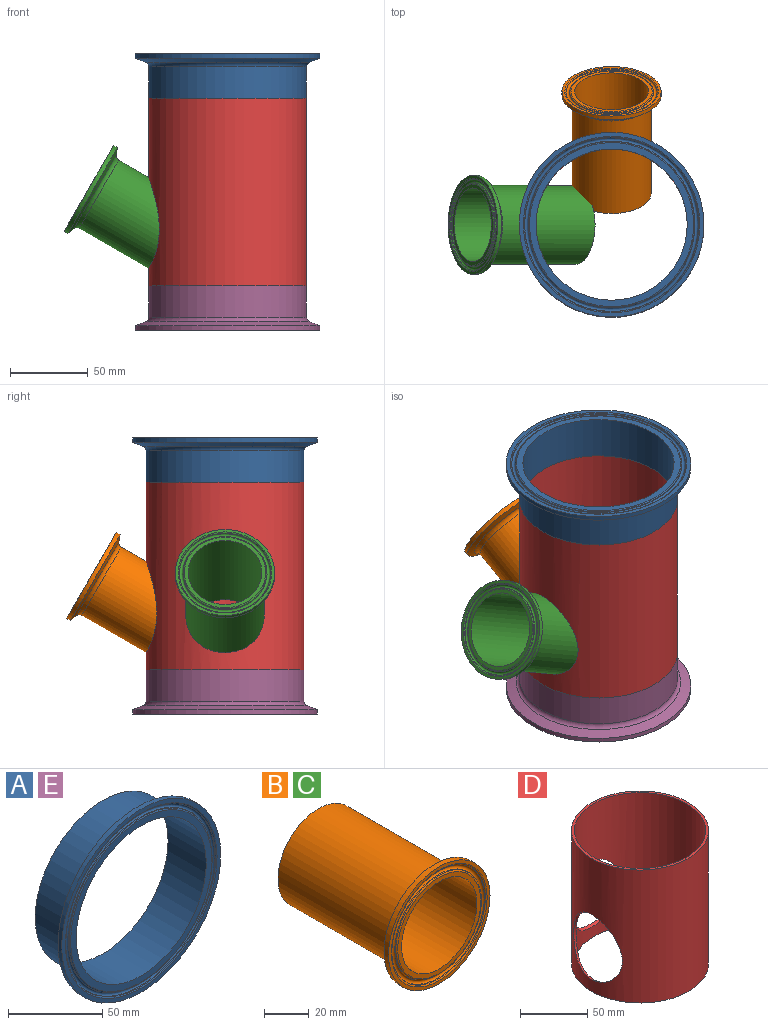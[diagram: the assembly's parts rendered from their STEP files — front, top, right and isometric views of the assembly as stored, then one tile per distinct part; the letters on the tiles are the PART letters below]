
ASSEMBLY  parts=5 mates=4
PART A: 13 faces, bbox 122.9x28.6x122.9 mm
  f0: cylinder r=59.46mm len=118.92mm, axis (0,-1,0), area 1062.8mm2, adj f1,f10
  f1: cone r=52.89mm half-angle=70deg, axis (0,-1,0), area 2468.6mm2, adj f0,f2
  f2: torus R=53.98mm, axis (0,-1,0), area 1256mm2, adj f1,f3
  f3: cylinder r=50.8mm len=101.6mm, axis (0,-1,0), area 6496.9mm2, adj f2,f12
  f4: cylinder r=48.69mm len=97.38mm, axis (0,-1,0), area 8742.2mm2, adj f11,f12
  f5: torus R=52.81mm, axis (0,-1,0), area 307.9mm2, adj f6,f11
  f6: cone r=53.7mm half-angle=23deg, axis (0,1,0), area 143.9mm2, adj f5,f7
  f7: torus R=54.8mm, axis (0,-1,0), area 961.3mm2, adj f6,f8
  f8: cone r=56.07mm half-angle=23deg, axis (0,-1,0), area 150.2mm2, adj f7,f9
  f9: torus R=56.79mm, axis (0,-1,0), area 326.2mm2, adj f8,f10
  f10: plane 118.92x118.92mm, normal (0,-1,0), area 975.3mm2, adj f0,f9
  f11: plane 105.62x105.62mm, normal (0,-1,0), area 1313.2mm2, adj f4,f5
  f12: plane 101.6x101.6mm, normal (0,1,0), area 658.9mm2, adj f3,f4
PART B: 13 faces, bbox 65.3x76.2x65.3 mm
  f0: cylinder r=31.95mm len=63.91mm, axis (0,-1,0), area 571.1mm2, adj f1,f10
  f1: cone r=27.49mm half-angle=70deg, axis (0,-1,0), area 887.1mm2, adj f0,f2
  f2: torus R=28.57mm, axis (0,-1,0), area 636.9mm2, adj f1,f3
  f3: cylinder r=25.4mm len=68.75mm, axis (0,-1,0), area 10971.5mm2, adj f2,f12
  f4: cylinder r=23.75mm len=76.2mm, axis (0,-1,0), area 11370.5mm2, adj f11,f12
  f5: torus R=26.18mm, axis (0,-1,0), area 153.8mm2, adj f6,f11
  f6: cone r=27.07mm half-angle=23deg, axis (0,1,0), area 72.4mm2, adj f5,f7
  f7: torus R=28.17mm, axis (0,-1,0), area 494.2mm2, adj f6,f8
  f8: cone r=29.43mm half-angle=23deg, axis (0,-1,0), area 78.8mm2, adj f7,f9
  f9: torus R=30.16mm, axis (0,-1,0), area 172.1mm2, adj f8,f10
  f10: plane 63.91x63.91mm, normal (0,-1,0), area 350.1mm2, adj f0,f9
  f11: plane 52.36x52.36mm, normal (0,-1,0), area 381mm2, adj f4,f5
  f12: plane 50.8x50.8mm, normal (0,1,0), area 254.9mm2, adj f3,f4
PART C: same geometry as B
PART D: 6 faces, bbox 127x127x120.7 mm
  f0: cylinder r=25.4mm len=59.89mm, axis (0.87,0,-0.5), area 418.5mm2, adj f1,f2
  f1: cylinder r=48.69mm len=120.65mm, axis (0,0,-1), area 32063.6mm2, adj f0,f3,f4,f5
  f2: cylinder r=50.8mm len=120.65mm, axis (0,0,-1), area 33676mm2, adj f0,f3,f4,f5
  f3: plane 101.6x101.6mm, normal (0,0,1), area 658.9mm2, adj f1,f2
  f4: plane 101.6x101.6mm, normal (0,0,-1), area 658.9mm2, adj f1,f2
  f5: cylinder r=25.4mm len=59.89mm, axis (0,-0.87,-0.5), area 418.5mm2, adj f1,f2
PART E: same geometry as A
PLACE A rot(axis=(-1,0,0),90deg) t=(0,0,177.8)mm
PLACE B rot(axis=(-0.69,0.19,-0.69),158.9deg) t=(0,85.98,89.21)mm
PLACE C rot(axis=(-0.77,-0.45,-0.45),104.5deg) t=(-89.35,0,91.16)mm
PLACE D t=(0,0,28.58)mm
PLACE E rot(axis=(1,0,0),90deg) t=(0,0,0)mm
MATE fastened D.f2 <-> A.f0  axis (0,0,1) through (0,0,149.23)mm
MATE fastened D.f0 <-> C.f0  axis (0.87,0,-0.5) through (-49.75,0,68.3)mm
MATE fastened D.f5 <-> B.f0  axis (0,-0.87,-0.5) through (0,49.75,68.3)mm
MATE fastened D.f2 <-> E.f0  axis (0,0,-1) through (0,0,28.58)mm
